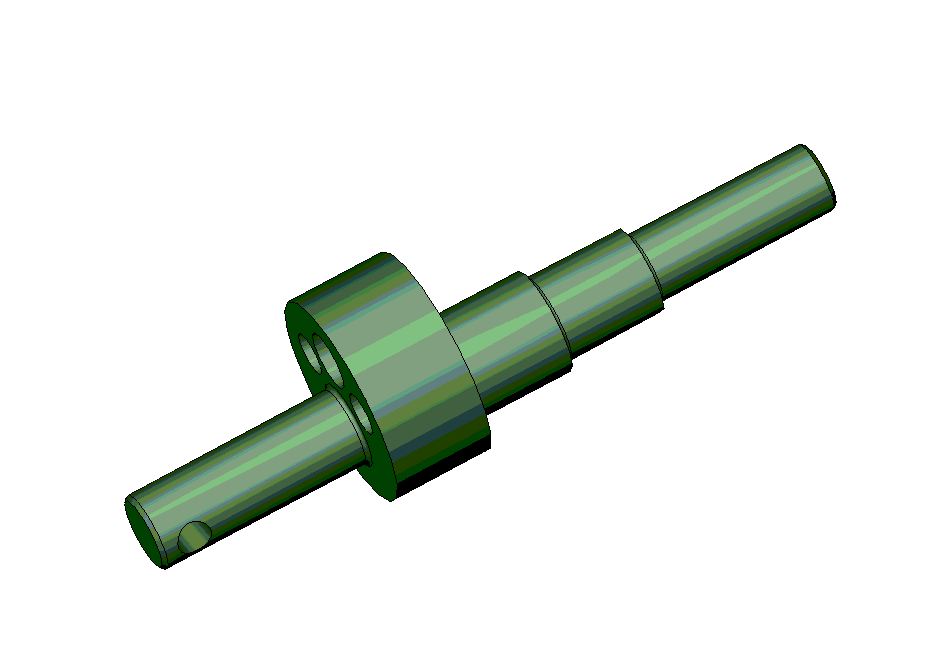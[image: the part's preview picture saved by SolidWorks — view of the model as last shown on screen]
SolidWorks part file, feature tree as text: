
SOLIDWORKS PART (.sldprt)
format: sldprt  version: not decoded by parser v0  size: 405,504 bytes
history: native  units: mm
features: sketch x8, plane x7, extrude x6, fillet x4, cut_extrude x2, chamfer x2, material x1 (+13 scaffold rows collapsed)
feature tree (43):
  scaffold x13  (default folders/planes/origin — collapsed)
  material  "Material <not specified>"
  extrude  "Boss-Extrude4"  [1 undecoded]
  sketch  "Sketch8"  dims[c1.D1=8.0mm c2.D1=8.0mm]
  extrude  "Boss-Extrude3"  [1 undecoded]
  sketch  "Sketch6"  dims[c1.D1=10.0mm c2.D1=11.8mm]
  extrude  "Boss-Extrude8"  [1 undecoded]
  sketch  "Sketch9"  dims[c1.D1=8.0mm c2.D1=14.0mm c2.RD1=25.2mm]
  extrude  "Base-Extrude"  [1 undecoded]
  sketch  "Sketch1"  dims[c1.D1=9.0mm c2.D1=25.2mm c2.RD2=11.5mm]
  extrude  "Boss-Extrude1"  [1 undecoded]
  sketch  "Sketch2"  dims[c1.D2=24.0mm c1.D8=6.8mm c1.D9=5.0mm c1.D10=5.0mm c1.D1=3.5mm c1.D3=6.0mm c1.D4=~17.809112mm c2.D4=45.0deg c2.D5=~17.897834mm c3.D5=45.0deg c3.D6=8.6mm c3.D4=~24.808775mm c4.D4=45.0deg c4.D5=~22.492079mm c5.D5=45.0deg c5.D6=8.6mm c5.D7=8.6mm c5.D1=11.5mm c5.RD3=12.5mm]
  extrude  "Boss-Extrude2"  [1 undecoded]
  sketch  "Sketch3"  dims[c1.D1=12.0mm c2.D1=12.5mm c2.RD4=11.8mm c2.RD5=8.0mm c2.RD6=14.0mm]
  plane  "Plane1"  Offset=0mm
  plane  "Plane2"  Offset=0mm
  plane  "Plane3"  Offset=4.5mm
  sketch  "Sketch4"  dims[D2=4.0mm D1=4.0mm]
  cut_extrude  "Cut-Extrude1"  [1 undecoded]
  plane  "Plane4"  Offset=0mm
  plane  "Plane5"  Offset=5mm
  sketch  "Sketch7"  dims[c1.D3=3.0mm c1.D4=3.0mm c2.D3=1.5mm c2.D4=1.5mm c2.D1=2.5mm c2.D2=6.0mm c2.D5=3.0mm c3.D4=3.0mm]
  cut_extrude  "Cut-Extrude2"  Depth=1.5mm
  plane  "Plane6"  Offset=0mm
  plane  "Plane7"  Offset=0mm
  chamfer  "Chamfer1"  Distance=0.5mm Angle=45deg
  fillet  "Fillet1"  Radius=0.5mm
  fillet  "Fillet2"  Radius=0.5mm
  fillet  "Fillet3"  Radius=0.5mm
  fillet  "Fillet4"  Radius=0.5mm
  chamfer  "Chamfer2"  Distance=0.5mm Angle=45deg
decode coverage: 15 of 22 modeling features carry decoded parameters
note: ~ marks probable driven/reference dimensions
note: 7 parameter values undecoded
summary: no parameter record found for 7 features
note: suppression state not decoded; provenance and decode notes live in map.json
